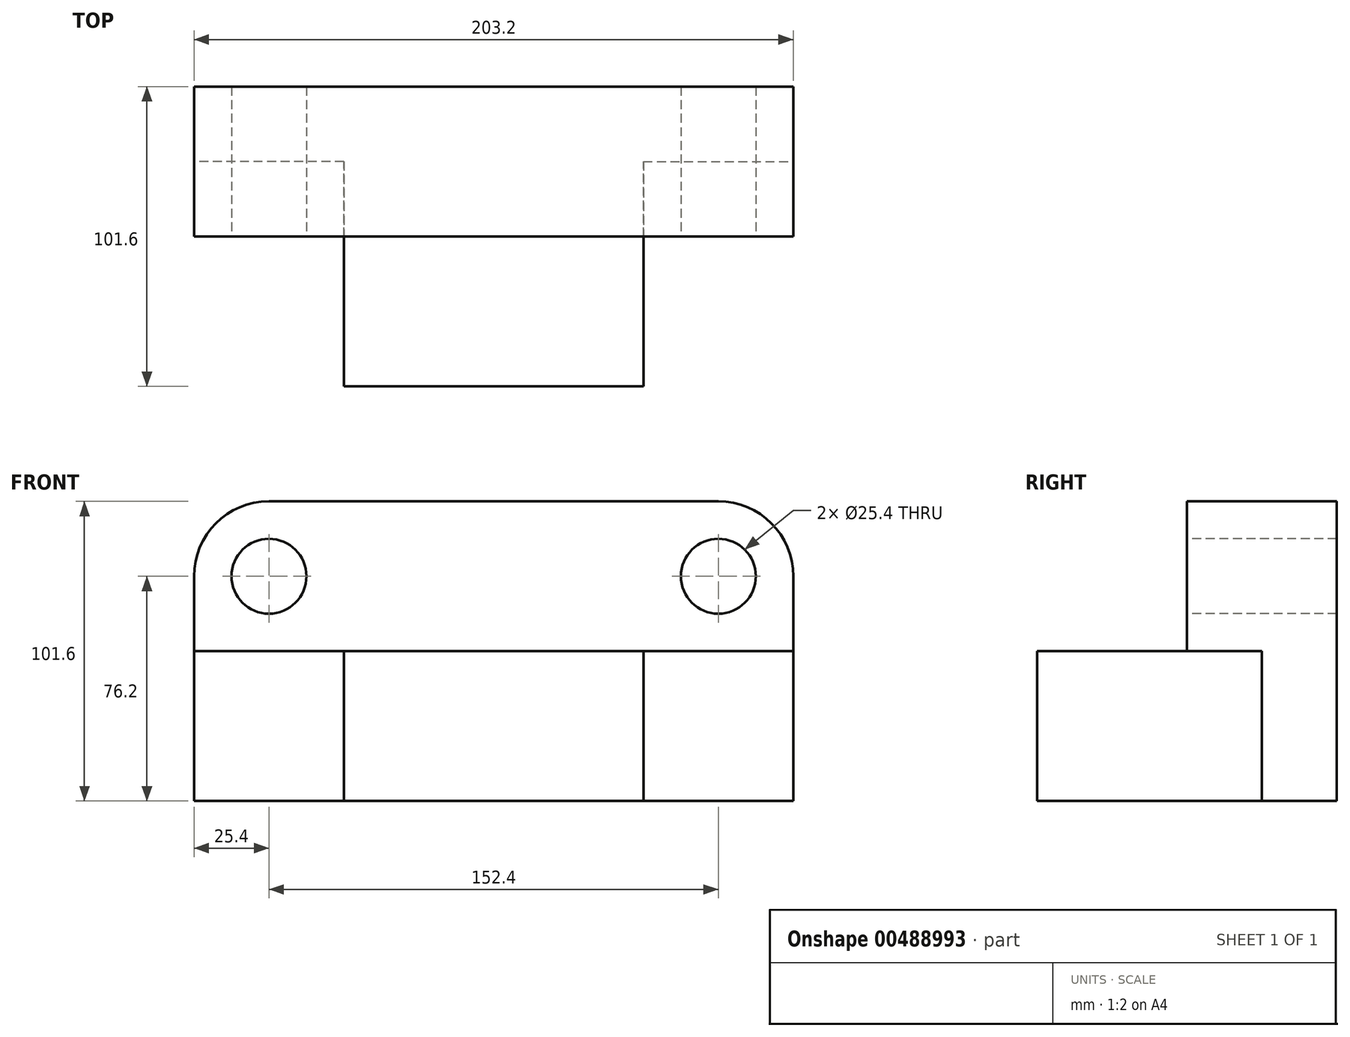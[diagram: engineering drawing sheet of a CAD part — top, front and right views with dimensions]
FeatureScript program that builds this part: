
annotation { "Feature Type Name" : "Feature", "Feature Type Description" : "" }
export const myFeature = defineFeature(function(context is Context, id is Id, definition is map)
    precondition{}
    {
        {
            var Q0;
            Q0=qCreatedBy(makeId("Top.planeOp"),FACE);
            var sketch = newSketch(context, id + "F0", { "sketchPlane" : qUnion([Q0])});
            skLineSegment(sketch, "E0.bottom", {"start": v(-107.65, 61.42) * mm, "end": v(95.55, 61.42) * mm});
            skLineSegment(sketch, "E0.top", {"start": v(-107.65, -40.18) * mm, "end": v(95.55, -40.18) * mm});
            skLineSegment(sketch, "E0.left", {"start": v(-107.65, 61.42) * mm, "end": v(-107.65, -40.18) * mm});
            skLineSegment(sketch, "E0.right", {"start": v(95.55, 61.42) * mm, "end": v(95.55, -40.18) * mm});
            skSolve(sketch);
        }
        {
            var Q0;
            Q0 = qSketchRegion(id + "F0", true);
            extrude(context, id + "F1", {"entities" : qUnion([Q0]), "depth" : 101.6 * mm});
        }
        {
            var Q0;
            Q0=makeQuery(id+"F1.opExtrude","SWEPT_FACE",FACE,{"disambiguationData":[OSD([sQuery(id+"F0.wireOp",EDGE,"E0.top")])]});
            var sketch = newSketch(context, id + "F2", { "sketchPlane" : qUnion([Q0])});
            skLineSegment(sketch, "E1.bottom", {"start": v(-107.65, 101.6) * mm, "end": v(95.55, 101.6) * mm});
            skLineSegment(sketch, "E1.top", {"start": v(-107.65, 50.8) * mm, "end": v(95.55, 50.8) * mm});
            skLineSegment(sketch, "E1.left", {"start": v(-107.65, 101.6) * mm, "end": v(-107.65, 50.8) * mm});
            skLineSegment(sketch, "E1.right", {"start": v(95.55, 101.6) * mm, "end": v(95.55, 50.8) * mm});
            skSolve(sketch);
        }
        {
            var Q0;
            Q0=makeQuery(id+"F1.opExtrude","SWEPT_FACE",FACE,{"disambiguationData":[OSD([sQuery(id+"F0.wireOp",EDGE,"E0.right")])]});
            var sketch = newSketch(context, id + "F3", { "sketchPlane" : qUnion([Q0])});
            skLineSegment(sketch, "E2.bottom", {"start": v(-40.18, 0) * mm, "end": v(36.02, 0) * mm});
            skLineSegment(sketch, "E2.top", {"start": v(-40.18, 50.8) * mm, "end": v(36.02, 50.8) * mm});
            skLineSegment(sketch, "E2.left", {"start": v(-40.18, 0) * mm, "end": v(-40.18, 50.8) * mm});
            skLineSegment(sketch, "E2.right", {"start": v(36.02, 0) * mm, "end": v(36.02, 50.8) * mm});
            skSolve(sketch);
        }
        {
            var Q0;
            Q0 = qSketchRegion(id + "F3", true);
            extrude(context, id + "F4", {"entities" : qUnion([Q0]), "operationType" : NewBodyOperationType.REMOVE, "oppositeDirection" : true, "depth" : 50.8 * mm});
        }
        {
            var Q0;
            Q0=makeQuery(id+"F1.opExtrude","SWEPT_FACE",FACE,{"disambiguationData":[OSD([sQuery(id+"F0.wireOp",EDGE,"E0.left")])]});
            var sketch = newSketch(context, id + "F5", { "sketchPlane" : qUnion([Q0])});
            skLineSegment(sketch, "E3.bottom", {"start": v(40.18, 0) * mm, "end": v(-36.02, 0) * mm});
            skLineSegment(sketch, "E3.top", {"start": v(40.18, 50.8) * mm, "end": v(-36.02, 50.8) * mm});
            skLineSegment(sketch, "E3.left", {"start": v(40.18, 0) * mm, "end": v(40.18, 50.8) * mm});
            skLineSegment(sketch, "E3.right", {"start": v(-36.02, 0) * mm, "end": v(-36.02, 50.8) * mm});
            skSolve(sketch);
        }
        {
            var Q0;
            Q0 = qSketchRegion(id + "F5", true);
            extrude(context, id + "F6", {"entities" : qUnion([Q0]), "operationType" : NewBodyOperationType.REMOVE, "oppositeDirection" : true, "depth" : 50.8 * mm});
        }
        {
            var Q0;
            Q0 = qSketchRegion(id + "F2", true);
            extrude(context, id + "F7", {"entities" : qUnion([Q0]), "operationType" : NewBodyOperationType.REMOVE, "oppositeDirection" : true, "depth" : 50.8 * mm});
        }
        {
            var Q0;
            Q0=makeQuery(id+"F1.opExtrude","CAP_EDGE",EDGE,{"disambiguationData":[OSD([sQuery(id+"F0.wireOp",EDGE,"E0.right")])],"isStart":false});
            var Q1;
            Q1=makeQuery(id+"F1.opExtrude","CAP_EDGE",EDGE,{"disambiguationData":[OSD([sQuery(id+"F0.wireOp",EDGE,"E0.left")])],"isStart":false});
            fillet(context, id + "F8", {"entities" : qUnion([Q0, Q1]), "radius" : 25.4 * mm, "tangentPropagation" : true, "allowEdgeOverflow" : false});
        }
        {
            var Q0;
            Q0=makeQuery(id+"F7.boolean.opBoolean","COPY",FACE,{"derivedFrom":makeQuery(id+"F7.opExtrude","CAP_FACE",FACE,{"disambiguationData":[OSD([sQuery(id+"F2.wireOp",EDGE,"E1.bottom"),sQuery(id+"F2.wireOp",EDGE,"E1.top"),sQuery(id+"F2.wireOp",EDGE,"E1.left"),sQuery(id+"F2.wireOp",EDGE,"E1.right")])],"isStart":false})});
            var sketch = newSketch(context, id + "F9", { "sketchPlane" : qUnion([Q0])});
            skCircle(sketch, "E4", {"center": v(-82.25, 76.2) * mm, "radius": 12.7 * mm});
            skCircle(sketch, "E5", {"center": v(70.15, 76.2) * mm, "radius": 12.7 * mm});
            skSolve(sketch);
        }
        {
            var Q0;
            Q0 = qSketchRegion(id + "F9", true);
            extrude(context, id + "F10", {"entities" : qUnion([Q0]), "operationType" : NewBodyOperationType.REMOVE, "endBound" : BoundingType.THROUGH_ALL, "oppositeDirection" : true, "depth" : 25.4 * mm});
        }
    });
